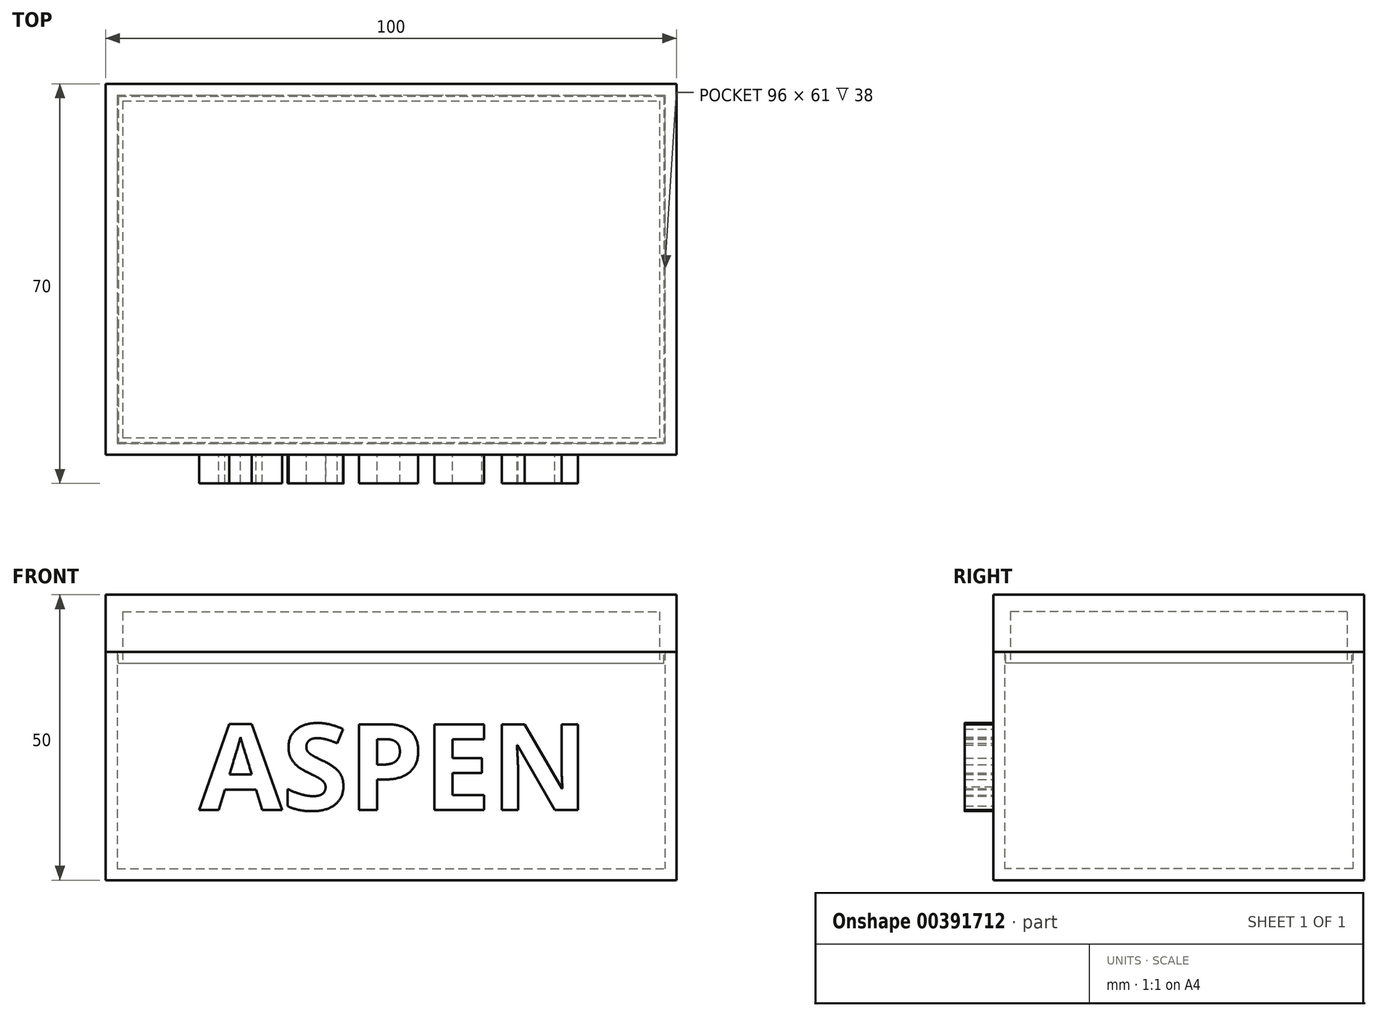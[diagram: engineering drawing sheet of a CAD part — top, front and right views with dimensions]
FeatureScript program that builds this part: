
annotation { "Feature Type Name" : "Feature", "Feature Type Description" : "" }
export const myFeature = defineFeature(function(context is Context, id is Id, definition is map)
    precondition{}
    {
        {
            var Q0;
            Q0=qCreatedBy(makeId("Top.planeOp"),FACE);
            var sketch = newSketch(context, id + "F0", { "sketchPlane" : qUnion([Q0])});
            skLineSegment(sketch, "E0.bottom", {"start": v(-75.62, 49.11) * mm, "end": v(24.38, 49.11) * mm});
            skLineSegment(sketch, "E0.top", {"start": v(-75.62, -15.89) * mm, "end": v(24.38, -15.89) * mm});
            skLineSegment(sketch, "E0.left", {"start": v(-75.62, 49.11) * mm, "end": v(-75.62, -15.89) * mm});
            skLineSegment(sketch, "E0.right", {"start": v(24.38, 49.11) * mm, "end": v(24.38, -15.89) * mm});
            skSolve(sketch);
        }
        {
            var Q0;
            Q0 = qSketchRegion(id + "F0", true);
            extrude(context, id + "F1", {"entities" : qUnion([Q0]), "depth" : 40 * mm});
        }
        {
            var Q0;
            Q0=makeQuery(id+"F1.opExtrude","CAP_FACE",FACE,{"disambiguationData":[OSD([sQuery(id+"F0.wireOp",EDGE,"E0.bottom"),sQuery(id+"F0.wireOp",EDGE,"E0.top"),sQuery(id+"F0.wireOp",EDGE,"E0.left"),sQuery(id+"F0.wireOp",EDGE,"E0.right")])],"isStart":false});
            shell(context, id + "F2", {"entities" : qUnion([Q0]), "thickness" : 2 * mm});
        }
        {
            var Q0;
            Q0=makeQuery(id+"F1.opExtrude","CAP_FACE",FACE,{"disambiguationData":[OSD([sQuery(id+"F0.wireOp",EDGE,"E0.bottom"),sQuery(id+"F0.wireOp",EDGE,"E0.top"),sQuery(id+"F0.wireOp",EDGE,"E0.left"),sQuery(id+"F0.wireOp",EDGE,"E0.right")])],"isStart":false});
            var sketch = newSketch(context, id + "F3", { "sketchPlane" : qUnion([Q0])});
            skLineSegment(sketch, "E1.0", {"start": v(-75.62, 49.11) * mm, "end": v(-75.62, -15.89) * mm});
            skLineSegment(sketch, "E1.1", {"start": v(-75.62, -15.89) * mm, "end": v(24.38, -15.89) * mm});
            skLineSegment(sketch, "E1.2", {"start": v(24.38, 49.11) * mm, "end": v(24.38, -15.89) * mm});
            skLineSegment(sketch, "E1.3", {"start": v(-75.62, 49.11) * mm, "end": v(24.38, 49.11) * mm});
            skSolve(sketch);
        }
        {
            var Q0;
            Q0 = qSketchRegion(id + "F3", true);
            extrude(context, id + "F4", {"entities" : qUnion([Q0]), "depth" : 10 * mm});
        }
        {
            var Q0;
            Q0=makeQuery(id+"F4.opExtrude","CAP_FACE",FACE,{"disambiguationData":[OSD([sQuery(id+"F3.wireOp",EDGE,"E1.0"),sQuery(id+"F3.wireOp",EDGE,"E1.1"),sQuery(id+"F3.wireOp",EDGE,"E1.2"),sQuery(id+"F3.wireOp",EDGE,"E1.3")])],"isStart":true});
            shell(context, id + "F5", {"entities" : qUnion([Q0]), "thickness" : 3 * mm});
        }
        {
            var Q0;
            Q0=makeQuery(id+"F4.opExtrude","CAP_FACE",FACE,{"disambiguationData":[OSD([sQuery(id+"F3.wireOp",EDGE,"E1.0"),sQuery(id+"F3.wireOp",EDGE,"E1.1"),sQuery(id+"F3.wireOp",EDGE,"E1.2"),sQuery(id+"F3.wireOp",EDGE,"E1.3")])],"isStart":true});
            var sketch = newSketch(context, id + "F6", { "sketchPlane" : qUnion([Q0])});
            skLineSegment(sketch, "E2.0", {"start": v(-72.62, -46.11) * mm, "end": v(-72.62, 12.89) * mm});
            skLineSegment(sketch, "E2.1", {"start": v(-72.62, 12.89) * mm, "end": v(21.38, 12.89) * mm});
            skLineSegment(sketch, "E2.2", {"start": v(21.38, -46.11) * mm, "end": v(21.38, 12.89) * mm});
            skLineSegment(sketch, "E2.3", {"start": v(-72.62, -46.11) * mm, "end": v(21.38, -46.11) * mm});
            skLineSegment(sketch, "E3.0", {"start": v(-73.42, 13.69) * mm, "end": v(22.18, 13.69) * mm});
            skLineSegment(sketch, "E3.1", {"start": v(-73.42, -46.91) * mm, "end": v(-73.42, 13.69) * mm});
            skLineSegment(sketch, "E3.2", {"start": v(-73.42, -46.91) * mm, "end": v(22.18, -46.91) * mm});
            skLineSegment(sketch, "E3.3", {"start": v(22.18, -46.91) * mm, "end": v(22.18, 13.69) * mm});
            skSolve(sketch);
        }
        {
            var Q0;
            Q0 = qSketchRegion(id + "F6", true);
            extrude(context, id + "F7", {"entities" : qUnion([Q0]), "operationType" : NewBodyOperationType.ADD, "depth" : 2 * mm});
        }
        {
            var Q0;
            Q0=makeQuery(id+"F1.opExtrude","SWEPT_FACE",FACE,{"disambiguationData":[OSD([sQuery(id+"F0.wireOp",EDGE,"E0.top")])]});
            var sketch = newSketch(context, id + "F8", { "sketchPlane" : qUnion([Q0])});
            skLineSegment(sketch, "E4", {"start": v(-25.62, 40) * mm, "end": v(-25.62, 0) * mm, "construction": true});
            skLineSegment(sketch, "E5", {"start": v(24.38, 20) * mm, "end": v(-75.62, 20) * mm, "construction": true});
            skLineSegment(sketch, "E6.bottom", {"start": v(-65.62, 30) * mm, "end": v(14.38, 30) * mm});
            skLineSegment(sketch, "E6.top", {"start": v(-65.62, 10) * mm, "end": v(14.38, 10) * mm});
            skLineSegment(sketch, "E6.left", {"start": v(-65.62, 30) * mm, "end": v(-65.62, 10) * mm});
            skLineSegment(sketch, "E6.right", {"start": v(14.38, 30) * mm, "end": v(14.38, 10) * mm});
            skSolve(sketch);
        }
        {
            var Q0;
            Q0=makeQuery(id+"F8.imprint","IMPRINT",FACE,{"disambiguationData":[TD([[makeQuery(id+"F8.imprint","IMPRINT",EDGE,{"derivedFrom":sQuery(id+"F8.wireOp",EDGE,"E6.bottom")}),1.0]])]});
            var sketch = newSketch(context, id + "F9", { "sketchPlane" : qUnion([Q0])});
            skText(sketch, "E7", { "text": "ASPEN", "fontName": "OpenSans-Bold.ttf"});
            skLineSegment(sketch, "E8", {"start": v(-65.62, 20) * mm, "end": v(14.38, 20) * mm, "construction": true});
            skLineSegment(sketch, "E9", {"start": v(-25.62, 30) * mm, "end": v(-25.4, 10) * mm, "construction": true});
            const initialGuessF9  = {"E7": [-0.05926, 0.01228, 1, 0, 0.01516]};
            skSetInitialGuess(sketch, initialGuessF9);
            skSolve(sketch);
        }
        {
            var Q0;
            Q0 = qSketchRegion(id + "F9", true);
            extrude(context, id + "F10", {"entities" : qUnion([Q0]), "operationType" : NewBodyOperationType.ADD, "depth" : 5 * mm});
        }
    });
